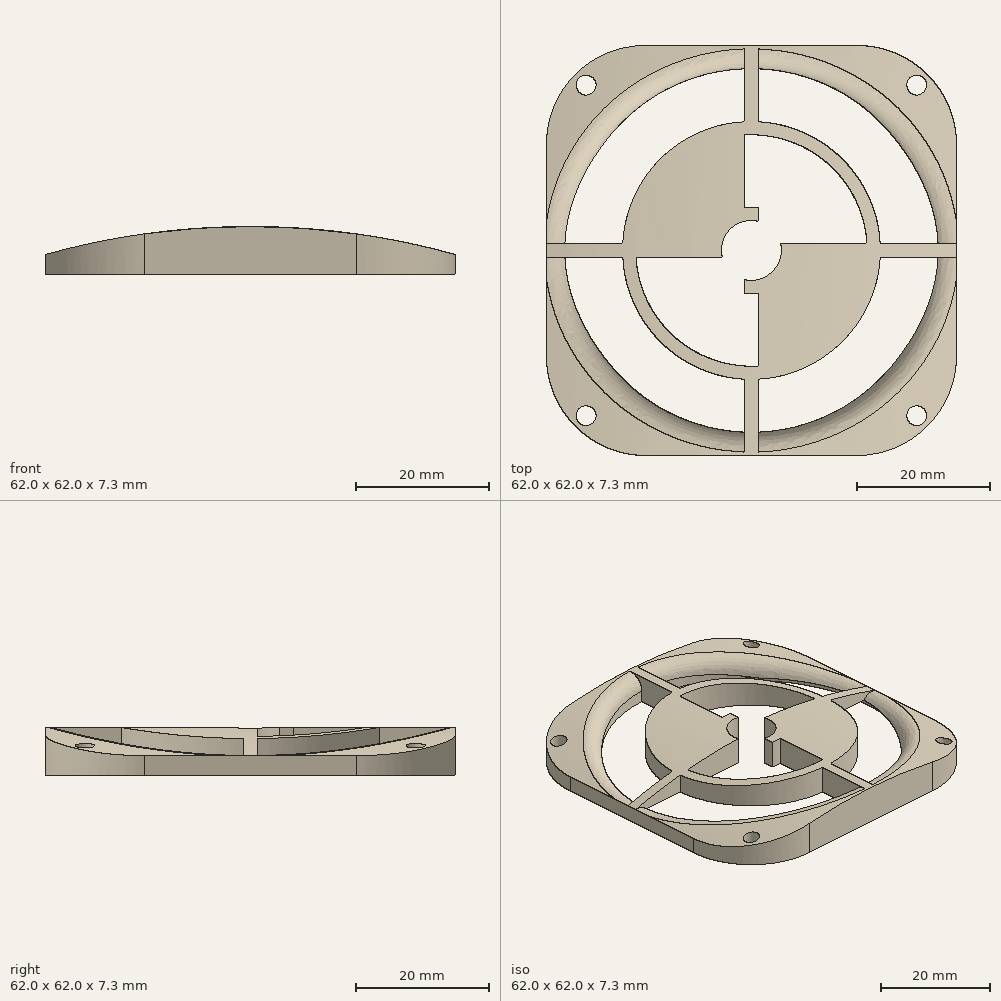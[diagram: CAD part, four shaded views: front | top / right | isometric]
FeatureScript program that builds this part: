
annotation { "Feature Type Name" : "Feature", "Feature Type Description" : "" }
export const myFeature = defineFeature(function(context is Context, id is Id, definition is map)
    precondition{}
    {
        {
            var Q0;
            Q0=qCreatedBy(makeId("Top.planeOp"),FACE);
            var sketch = newSketch(context, id + "F0", { "sketchPlane" : qUnion([Q0])});
            skLineSegment(sketch, "E0", {"start": v(0, 70.57) * mm, "end": v(0, -91.76) * mm, "construction": true});
            skLineSegment(sketch, "E1", {"start": v(-109.37, 0) * mm, "end": v(112.01, 0) * mm, "construction": true});
            skCircle(sketch, "E2", {"center": v(0, 0) * mm, "radius": 27.5 * mm});
            skLineSegment(sketch, "E3.bottom", {"start": v(31, 31) * mm, "end": v(-31, 31) * mm});
            skLineSegment(sketch, "E3.top", {"start": v(31, -31) * mm, "end": v(-31, -31) * mm});
            skLineSegment(sketch, "E3.left", {"start": v(31, 31) * mm, "end": v(31, -31) * mm});
            skLineSegment(sketch, "E3.right", {"start": v(-31, 31) * mm, "end": v(-31, -31) * mm});
            skLineSegment(sketch, "E4.bottom", {"start": v(25, 25) * mm, "end": v(-25, 25) * mm, "construction": true});
            skLineSegment(sketch, "E4.top", {"start": v(25, -25) * mm, "end": v(-25, -25) * mm, "construction": true});
            skLineSegment(sketch, "E4.left", {"start": v(25, 25) * mm, "end": v(25, -25) * mm, "construction": true});
            skLineSegment(sketch, "E4.right", {"start": v(-25, 25) * mm, "end": v(-25, -25) * mm, "construction": true});
            skCircle(sketch, "E5", {"center": v(25, 25) * mm, "radius": 1.5 * mm});
            skCircle(sketch, "E6.MirrorC", {"center": v(-25, 25) * mm, "radius": 1.5 * mm});
            skCircle(sketch, "E7.MirrorC", {"center": v(25, -25) * mm, "radius": 1.5 * mm});
            skCircle(sketch, "E8.MirrorC", {"center": v(-25, -25) * mm, "radius": 1.5 * mm});
            skCircle(sketch, "E9", {"center": v(0, 0) * mm, "radius": 6.52 * mm});
            skCircle(sketch, "E10.0", {"center": v(0, 0) * mm, "radius": 4.52 * mm});
            skCircle(sketch, "E11", {"center": v(0, 0) * mm, "radius": 17.5 * mm});
            skCircle(sketch, "E12.0", {"center": v(0, 0) * mm, "radius": 19.5 * mm});
            skLineSegment(sketch, "E13", {"start": v(-27.48, -1) * mm, "end": v(27.48, -1) * mm});
            skLineSegment(sketch, "E14.MirrorCS", {"start": v(-27.48, 1) * mm, "end": v(27.48, 1) * mm});
            skLineSegment(sketch, "E15", {"start": v(1, 27.48) * mm, "end": v(1, -27.48) * mm});
            skLineSegment(sketch, "E16.MirrorCS", {"start": v(-1, 27.48) * mm, "end": v(-1, -27.48) * mm});
            skSolve(sketch);
        }
        {
            var Q0;
            Q0=qSketchRegion(id+"F0",true);
            var Q1;
            {var subQ0=sQuery(id+"F0.wireOp",EDGE,"E16.MirrorCS");var subQ1=sQuery(id+"F0.wireOp",EDGE,"E11");var subQ2=makeQuery(id+"F0.imprint","INTERSECT",VERTEX,{"disambiguationData":[OD(0.0)],"derivedFrom":[subQ1,subQ0]});Q1=makeQuery(id+"F0.imprint","IMPRINT",FACE,{"disambiguationData":[TD([[makeQuery(id+"F0.imprint","IMPRINT",EDGE,{"disambiguationData":[TD([[subQ2,-1.0]])],"derivedFrom":subQ1}),-1.0]])]});}
            var Q2;
            {var subQ0=sQuery(id+"F0.wireOp",EDGE,"E13");var subQ1=sQuery(id+"F0.wireOp",EDGE,"E2");var subQ2=makeQuery(id+"F0.imprint","INTERSECT",VERTEX,{"disambiguationData":[OD(0.0)],"derivedFrom":[subQ1,subQ0]});Q2=makeQuery(id+"F0.imprint","IMPRINT",FACE,{"disambiguationData":[TD([[makeQuery(id+"F0.imprint","IMPRINT",EDGE,{"disambiguationData":[TD([[subQ2,1.0]])],"derivedFrom":subQ1}),1.0]])]});}
            var Q3;
            {var subQ0=sQuery(id+"F0.wireOp",EDGE,"E13");var subQ1=sQuery(id+"F0.wireOp",EDGE,"E11");var subQ2=makeQuery(id+"F0.imprint","INTERSECT",VERTEX,{"disambiguationData":[OD(0.0)],"derivedFrom":[subQ1,subQ0]});Q3=makeQuery(id+"F0.imprint","IMPRINT",FACE,{"disambiguationData":[TD([[makeQuery(id+"F0.imprint","IMPRINT",EDGE,{"disambiguationData":[TD([[subQ2,-1.0]])],"derivedFrom":subQ1}),-1.0]])]});}
            var Q4;
            {var subQ0=sQuery(id+"F0.wireOp",EDGE,"E14.MirrorCS");var subQ1=sQuery(id+"F0.wireOp",EDGE,"E9");var subQ2=makeQuery(id+"F0.imprint","INTERSECT",VERTEX,{"disambiguationData":[OD(1.0)],"derivedFrom":[subQ1,subQ0]});Q4=makeQuery(id+"F0.imprint","IMPRINT",FACE,{"disambiguationData":[TD([[makeQuery(id+"F0.imprint","IMPRINT",EDGE,{"disambiguationData":[TD([[subQ2,-1.0]])],"derivedFrom":subQ1}),-1.0]])]});}
            var Q5;
            {var subQ0=sQuery(id+"F0.wireOp",EDGE,"E14.MirrorCS");var subQ1=sQuery(id+"F0.wireOp",EDGE,"E11");var subQ2=makeQuery(id+"F0.imprint","INTERSECT",VERTEX,{"disambiguationData":[OD(1.0)],"derivedFrom":[subQ1,subQ0]});Q5=makeQuery(id+"F0.imprint","IMPRINT",FACE,{"disambiguationData":[TD([[makeQuery(id+"F0.imprint","IMPRINT",EDGE,{"disambiguationData":[TD([[subQ2,-1.0]])],"derivedFrom":subQ1}),-1.0]])]});}
            var Q6;
            {var subQ0=sQuery(id+"F0.wireOp",EDGE,"E13");var subQ1=sQuery(id+"F0.wireOp",EDGE,"E9");var subQ2=makeQuery(id+"F0.imprint","INTERSECT",VERTEX,{"disambiguationData":[OD(0.0)],"derivedFrom":[subQ1,subQ0]});Q6=makeQuery(id+"F0.imprint","IMPRINT",FACE,{"disambiguationData":[TD([[makeQuery(id+"F0.imprint","IMPRINT",EDGE,{"disambiguationData":[TD([[subQ2,-1.0]])],"derivedFrom":subQ1}),1.0]])]});}
            var Q7;
            {var subQ0=sQuery(id+"F0.wireOp",EDGE,"E14.MirrorCS");var subQ1=sQuery(id+"F0.wireOp",EDGE,"E9");var subQ2=makeQuery(id+"F0.imprint","INTERSECT",VERTEX,{"disambiguationData":[OD(1.0)],"derivedFrom":[subQ1,subQ0]});Q7=makeQuery(id+"F0.imprint","IMPRINT",FACE,{"disambiguationData":[TD([[makeQuery(id+"F0.imprint","IMPRINT",EDGE,{"disambiguationData":[TD([[subQ2,-1.0]])],"derivedFrom":subQ1}),1.0]])]});}
            var Q8;
            {var subQ0=sQuery(id+"F0.wireOp",EDGE,"E16.MirrorCS");var subQ1=sQuery(id+"F0.wireOp",EDGE,"E9");var subQ2=makeQuery(id+"F0.imprint","INTERSECT",VERTEX,{"disambiguationData":[OD(0.0)],"derivedFrom":[subQ1,subQ0]});Q8=makeQuery(id+"F0.imprint","IMPRINT",FACE,{"disambiguationData":[TD([[makeQuery(id+"F0.imprint","IMPRINT",EDGE,{"disambiguationData":[TD([[subQ2,-1.0]])],"derivedFrom":subQ1}),1.0]])]});}
            var Q9;
            {var subQ0=sQuery(id+"F0.wireOp",EDGE,"E15");var subQ1=sQuery(id+"F0.wireOp",EDGE,"E9");var subQ2=makeQuery(id+"F0.imprint","INTERSECT",VERTEX,{"disambiguationData":[OD(0.0)],"derivedFrom":[subQ1,subQ0]});Q9=makeQuery(id+"F0.imprint","IMPRINT",FACE,{"disambiguationData":[TD([[makeQuery(id+"F0.imprint","IMPRINT",EDGE,{"disambiguationData":[TD([[subQ2,-1.0]])],"derivedFrom":subQ1}),1.0]])]});}
            var Q10;
            {var subQ0=sQuery(id+"F0.wireOp",EDGE,"E15");var subQ1=sQuery(id+"F0.wireOp",EDGE,"E9");var subQ2=makeQuery(id+"F0.imprint","INTERSECT",VERTEX,{"disambiguationData":[OD(0.0)],"derivedFrom":[subQ1,subQ0]});Q10=makeQuery(id+"F0.imprint","IMPRINT",FACE,{"disambiguationData":[TD([[makeQuery(id+"F0.imprint","IMPRINT",EDGE,{"disambiguationData":[TD([[subQ2,1.0]])],"derivedFrom":subQ1}),1.0]])]});}
            var Q11;
            {var subQ0=sQuery(id+"F0.wireOp",EDGE,"E14.MirrorCS");var subQ1=sQuery(id+"F0.wireOp",EDGE,"E9");var subQ2=makeQuery(id+"F0.imprint","INTERSECT",VERTEX,{"disambiguationData":[OD(0.0)],"derivedFrom":[subQ1,subQ0]});Q11=makeQuery(id+"F0.imprint","IMPRINT",FACE,{"disambiguationData":[TD([[makeQuery(id+"F0.imprint","IMPRINT",EDGE,{"disambiguationData":[TD([[subQ2,1.0]])],"derivedFrom":subQ1}),1.0]])]});}
            var Q12;
            {var subQ0=sQuery(id+"F0.wireOp",EDGE,"E15");var subQ1=sQuery(id+"F0.wireOp",EDGE,"E9");var subQ2=makeQuery(id+"F0.imprint","INTERSECT",VERTEX,{"disambiguationData":[OD(1.0)],"derivedFrom":[subQ1,subQ0]});Q12=makeQuery(id+"F0.imprint","IMPRINT",FACE,{"disambiguationData":[TD([[makeQuery(id+"F0.imprint","IMPRINT",EDGE,{"disambiguationData":[TD([[subQ2,-1.0]])],"derivedFrom":subQ1}),1.0]])]});}
            var Q13;
            {var subQ0=sQuery(id+"F0.wireOp",EDGE,"E16.MirrorCS");var subQ1=sQuery(id+"F0.wireOp",EDGE,"E11");var subQ2=makeQuery(id+"F0.imprint","INTERSECT",VERTEX,{"disambiguationData":[OD(1.0)],"derivedFrom":[subQ1,subQ0]});Q13=makeQuery(id+"F0.imprint","IMPRINT",FACE,{"disambiguationData":[TD([[makeQuery(id+"F0.imprint","IMPRINT",EDGE,{"disambiguationData":[TD([[subQ2,-1.0]])],"derivedFrom":subQ1}),-1.0]])]});}
            var Q14;
            {var subQ0=sQuery(id+"F0.wireOp",EDGE,"E15");var subQ1=sQuery(id+"F0.wireOp",EDGE,"E2");var subQ2=makeQuery(id+"F0.imprint","INTERSECT",VERTEX,{"disambiguationData":[OD(1.0)],"derivedFrom":[subQ1,subQ0]});Q14=makeQuery(id+"F0.imprint","IMPRINT",FACE,{"disambiguationData":[TD([[makeQuery(id+"F0.imprint","IMPRINT",EDGE,{"disambiguationData":[TD([[subQ2,1.0]])],"derivedFrom":subQ1}),1.0]])]});}
            var Q15;
            {var subQ0=sQuery(id+"F0.wireOp",EDGE,"E16.MirrorCS");var subQ1=sQuery(id+"F0.wireOp",EDGE,"E9");var subQ2=makeQuery(id+"F0.imprint","INTERSECT",VERTEX,{"disambiguationData":[OD(1.0)],"derivedFrom":[subQ1,subQ0]});Q15=makeQuery(id+"F0.imprint","IMPRINT",FACE,{"disambiguationData":[TD([[makeQuery(id+"F0.imprint","IMPRINT",EDGE,{"disambiguationData":[TD([[subQ2,-1.0]])],"derivedFrom":subQ1}),-1.0]])]});}
            var Q16;
            {var subQ0=sQuery(id+"F0.wireOp",EDGE,"E15");var subQ1=sQuery(id+"F0.wireOp",EDGE,"E11");var subQ2=makeQuery(id+"F0.imprint","INTERSECT",VERTEX,{"disambiguationData":[OD(1.0)],"derivedFrom":[subQ1,subQ0]});Q16=makeQuery(id+"F0.imprint","IMPRINT",FACE,{"disambiguationData":[TD([[makeQuery(id+"F0.imprint","IMPRINT",EDGE,{"disambiguationData":[TD([[subQ2,-1.0]])],"derivedFrom":subQ1}),-1.0]])]});}
            var Q17;
            {var subQ0=sQuery(id+"F0.wireOp",EDGE,"E14.MirrorCS");var subQ1=sQuery(id+"F0.wireOp",EDGE,"E11");var subQ2=makeQuery(id+"F0.imprint","INTERSECT",VERTEX,{"disambiguationData":[OD(0.0)],"derivedFrom":[subQ1,subQ0]});Q17=makeQuery(id+"F0.imprint","IMPRINT",FACE,{"disambiguationData":[TD([[makeQuery(id+"F0.imprint","IMPRINT",EDGE,{"disambiguationData":[TD([[subQ2,1.0]])],"derivedFrom":subQ1}),-1.0]])]});}
            var Q18;
            {var subQ0=sQuery(id+"F0.wireOp",EDGE,"E14.MirrorCS");var subQ1=sQuery(id+"F0.wireOp",EDGE,"E9");var subQ2=makeQuery(id+"F0.imprint","INTERSECT",VERTEX,{"disambiguationData":[OD(0.0)],"derivedFrom":[subQ1,subQ0]});Q18=makeQuery(id+"F0.imprint","IMPRINT",FACE,{"disambiguationData":[TD([[makeQuery(id+"F0.imprint","IMPRINT",EDGE,{"disambiguationData":[TD([[subQ2,1.0]])],"derivedFrom":subQ1}),-1.0]])]});}
            var Q19;
            {var subQ0=sQuery(id+"F0.wireOp",EDGE,"E15");var subQ1=sQuery(id+"F0.wireOp",EDGE,"E11");var subQ2=makeQuery(id+"F0.imprint","INTERSECT",VERTEX,{"disambiguationData":[OD(0.0)],"derivedFrom":[subQ1,subQ0]});Q19=makeQuery(id+"F0.imprint","IMPRINT",FACE,{"disambiguationData":[TD([[makeQuery(id+"F0.imprint","IMPRINT",EDGE,{"disambiguationData":[TD([[subQ2,1.0]])],"derivedFrom":subQ1}),-1.0]])]});}
            var Q20;
            {var subQ0=sQuery(id+"F0.wireOp",EDGE,"E15");var subQ1=sQuery(id+"F0.wireOp",EDGE,"E11");var subQ2=makeQuery(id+"F0.imprint","INTERSECT",VERTEX,{"disambiguationData":[OD(0.0)],"derivedFrom":[subQ1,subQ0]});Q20=makeQuery(id+"F0.imprint","IMPRINT",FACE,{"disambiguationData":[TD([[makeQuery(id+"F0.imprint","IMPRINT",EDGE,{"disambiguationData":[TD([[subQ2,-1.0]])],"derivedFrom":subQ1}),-1.0]])]});}
            var Q21;
            {var subQ0=sQuery(id+"F0.wireOp",EDGE,"E15");var subQ1=sQuery(id+"F0.wireOp",EDGE,"E2");var subQ2=makeQuery(id+"F0.imprint","INTERSECT",VERTEX,{"disambiguationData":[OD(0.0)],"derivedFrom":[subQ1,subQ0]});Q21=makeQuery(id+"F0.imprint","IMPRINT",FACE,{"disambiguationData":[TD([[makeQuery(id+"F0.imprint","IMPRINT",EDGE,{"disambiguationData":[TD([[subQ2,-1.0]])],"derivedFrom":subQ1}),1.0]])]});}
            var Q22;
            {var subQ0=sQuery(id+"F0.wireOp",EDGE,"E15");var subQ1=sQuery(id+"F0.wireOp",EDGE,"E9");var subQ2=makeQuery(id+"F0.imprint","INTERSECT",VERTEX,{"disambiguationData":[OD(0.0)],"derivedFrom":[subQ1,subQ0]});Q22=makeQuery(id+"F0.imprint","IMPRINT",FACE,{"disambiguationData":[TD([[makeQuery(id+"F0.imprint","IMPRINT",EDGE,{"disambiguationData":[TD([[subQ2,-1.0]])],"derivedFrom":subQ1}),-1.0]])]});}
            var Q23;
            {var subQ0=sQuery(id+"F0.wireOp",EDGE,"E16.MirrorCS");var subQ1=sQuery(id+"F0.wireOp",EDGE,"E9");var subQ2=makeQuery(id+"F0.imprint","INTERSECT",VERTEX,{"disambiguationData":[OD(1.0)],"derivedFrom":[subQ1,subQ0]});Q23=makeQuery(id+"F0.imprint","IMPRINT",FACE,{"disambiguationData":[TD([[makeQuery(id+"F0.imprint","IMPRINT",EDGE,{"disambiguationData":[TD([[subQ2,-1.0]])],"derivedFrom":subQ1}),1.0]])]});}
            var Q24;
            {var subQ0=sQuery(id+"F0.wireOp",EDGE,"E13");var subQ1=sQuery(id+"F0.wireOp",EDGE,"E2");var subQ2=makeQuery(id+"F0.imprint","INTERSECT",VERTEX,{"disambiguationData":[OD(1.0)],"derivedFrom":[subQ1,subQ0]});Q24=makeQuery(id+"F0.imprint","IMPRINT",FACE,{"disambiguationData":[TD([[makeQuery(id+"F0.imprint","IMPRINT",EDGE,{"disambiguationData":[TD([[subQ2,-1.0]])],"derivedFrom":subQ1}),1.0]])]});}
            extrude(context, id + "F1", {"entities" : qUnion([Q0, Q1, Q2, Q3, Q4, Q5, Q6, Q7, Q8, Q9, Q10, Q11, Q12, Q13, Q14, Q15, Q16, Q17, Q18, Q19, Q20, Q21, Q22, Q23, Q24]), "depth" : 25 * mm, "offsetDistance" : 25 * mm});
        }
        {
            var Q0;
            Q0=makeQuery(id+"F1.opExtrude","SWEPT_FACE",FACE,{"disambiguationData":[OSD([sQuery(id+"F0.wireOp",EDGE,"E3.top")])]});
            var sketch = newSketch(context, id + "F2", { "sketchPlane" : qUnion([Q0])});
            skPoint(sketch, "E17", {"position": v(-31, 3) * mm});
            skPoint(sketch, "E18", {"position": v(31, 3) * mm});
            skCircle(sketch, "E19", {"center": v(0, -107.74) * mm, "radius": 115 * mm});
            skPoint(sketch, "E19.third.point", {"position": v(3.15, -222.7) * mm});
            skSolve(sketch);
        }
        {
            var Q0;
            {var subQ1=sQuery(id+"F0.wireOp",EDGE,"E3.top");var subQ6=makeQuery(id+"F1.opExtrude","CAP_EDGE",EDGE,{"disambiguationData":[OSD([subQ1])],"isStart":false});Q0=makeQuery(id+"F2.imprint","IMPRINT",FACE,{"disambiguationData":[TD([[makeQuery(id+"F2.imprint","IMPRINT",EDGE,{"derivedFrom":subQ6}),1.0]])]});}
            extrude(context, id + "F3", {"entities" : qUnion([Q0]), "operationType" : NewBodyOperationType.REMOVE, "oppositeDirection" : true, "depth" : 76 * mm});
        }
        {
            var Q0;
            Q0=makeQuery(id+"F1.opExtrude","SWEPT_EDGE",EDGE,{"disambiguationData":[OSD([sQuery(id+"F0.wireOp",EDGE,"E3.bottom"),sQuery(id+"F0.wireOp",EDGE,"E3.left")])]});
            var Q1;
            Q1=makeQuery(id+"F1.opExtrude","SWEPT_EDGE",EDGE,{"disambiguationData":[OSD([sQuery(id+"F0.wireOp",EDGE,"E3.top"),sQuery(id+"F0.wireOp",EDGE,"E3.left")])]});
            var Q2;
            Q2=makeQuery(id+"F1.opExtrude","SWEPT_EDGE",EDGE,{"disambiguationData":[OSD([sQuery(id+"F0.wireOp",EDGE,"E3.bottom"),sQuery(id+"F0.wireOp",EDGE,"E3.right")])]});
            var Q3;
            Q3=makeQuery(id+"F1.opExtrude","SWEPT_EDGE",EDGE,{"disambiguationData":[OSD([sQuery(id+"F0.wireOp",EDGE,"E3.top"),sQuery(id+"F0.wireOp",EDGE,"E3.right")])]});
            fillet(context, id + "F4", {"entities" : qUnion([Q0, Q1, Q2, Q3]), "radius" : 15 * mm, "tangentPropagation" : true, "allowEdgeOverflow" : false});
        }
        {
            var Q0;
            Q0=makeQuery(id+"F3.boolean.opBoolean","INTERSECT",EDGE,{"derivedFrom":[makeQuery(id+"F1.opExtrude","SWEPT_FACE",FACE,{"disambiguationData":[OSD([sQuery(id+"F0.wireOp",EDGE,"E2")])]}),makeQuery(id+"F3.opExtrude","SWEPT_FACE",FACE,{"disambiguationData":[OSD([sQuery(id+"F2.wireOp",EDGE,"E19")])]})]});
            fillet(context, id + "F5", {"entities" : qUnion([Q0]), "radius" : 3 * mm, "tangentPropagation" : true, "allowEdgeOverflow" : false});
        }
        {
            var Q0;
            Q0=makeQuery(id+"F1.opExtrude","CAP_FACE",FACE,{"disambiguationData":[OSD([sQuery(id+"F0.wireOp",EDGE,"E2"),sQuery(id+"F0.wireOp",EDGE,"E3.bottom"),sQuery(id+"F0.wireOp",EDGE,"E3.top"),sQuery(id+"F0.wireOp",EDGE,"E3.left"),sQuery(id+"F0.wireOp",EDGE,"E3.right"),sQuery(id+"F0.wireOp",EDGE,"E5"),sQuery(id+"F0.wireOp",EDGE,"E6.MirrorC"),sQuery(id+"F0.wireOp",EDGE,"E7.MirrorC"),sQuery(id+"F0.wireOp",EDGE,"E8.MirrorC"),sQuery(id+"F0.wireOp",EDGE,"E9"),sQuery(id+"F0.wireOp",EDGE,"E10.0"),sQuery(id+"F0.wireOp",EDGE,"E11"),sQuery(id+"F0.wireOp",EDGE,"E12.0"),sQuery(id+"F0.wireOp",EDGE,"E13"),sQuery(id+"F0.wireOp",EDGE,"E14.MirrorCS"),sQuery(id+"F0.wireOp",EDGE,"E15"),sQuery(id+"F0.wireOp",EDGE,"E16.MirrorCS")])],"isStart":true});
            var sketch = newSketch(context, id + "F6", { "sketchPlane" : qUnion([Q0])});
            skCircle(sketch, "E20", {"center": v(0, 0) * mm, "radius": 30 * mm});
            skSolve(sketch);
        }
        {
            var Q0;
            Q0=qSketchRegion(id+"F6",true);
            extrude(context, id + "F7", {"entities" : qUnion([Q0]), "operationType" : NewBodyOperationType.REMOVE, "oppositeDirection" : true, "depth" : 2 * mm, "offsetDistance" : 25 * mm});
        }
    });
